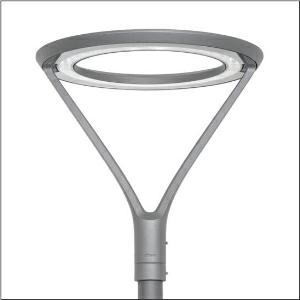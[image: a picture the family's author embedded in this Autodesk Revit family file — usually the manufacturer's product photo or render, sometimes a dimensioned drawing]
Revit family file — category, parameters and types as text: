
# Revit family: dl_r__20___pl1_2s_5xa512832s008_323f
name_source: partatom
category: Lighting Fixtures
units: mm (PartAtom-declared; Revit-internal decimal feet)

## family parameters
Cut with Voids When Loaded = No
Host = Face
Light Source = No
Part Type = Normal
Room Calculation Point = No
Round Connector Dimension = Use Diameter
Shared = No

## types (1)
- --- (1 x LED, 3050 lm, 30.4 W, 2200K)
    Apparent Load = 30 VA
    CIE Flux Codes = 33 78 99 100 100
    Color Rendering = 70
    Color Temperature = 2200K
    Default Elevation = 1800 mm
    Description = DL® 20, mast luminaire, primary light control with reflector, highly specular, primary optical cover: cover, of toughened safety glass of clear glass with excellent transmission level, light distribution: PL1.2s, light emission: direct distribution, primary light characteristic: symmetric, installation type: post-top, LED, High Power LED, rated luminous flux: 3.040lm, luminous efficacy: 86lm/W, light colour: 722, colour temperature: 2200K, control gear: ECG Plus, control: flexible luminous flux parameterisation, time-dependent luminous flux control, constant luminous flux control, digital communication interface, power reduction, overheat protection, electronic power reduction, mains connection: 230..240V, 50/60Hz, connection cable pre-assembled, cable length: 5m, start of lifetime: 36W, end of service life: 36W, reduction: 17W, luminaire housing, upper part, of cast aluminium, powder-coated, Siteco® metallic grey (DB 702S), diameter: 690mm, height: 690mm, spigot size: 76mm (post-top), luminaire housing, of cast aluminium, powder-coated, Siteco® metallic grey (DB 702S), equipment: standard, protection rating (complete): IP66, insulation class (complete): insulation class II (safety insulation), certification: CE, ENEC, VDE, impact resistance: IK08, permissible operating ambient temperature: -25..+35°C, standard-compliant lighting for roads and squares, packaging unit: 1 piece

Light Distribution: PL1.2s
    Height = 690 mm
    Lamp = 1 x LED
    Lamp Light Flux = 3050 lm
    Lamp Power = 30.4 W
    Lamp count = 1
    Length = 690 mm
    Luminous efficacy = 100 lm/W
    Manufacturer = Siteco
    ModVariant = No
    Model = 5XA512832S008
    Number of Poles = 1
    OnlyDefault = Yes
    Power Factor = 1
    Product Name = DL® 20 | PL1.2s
    Product group = mast luminaire | pylon top
    ProductGroupID = 6100
    Protection Class = Protection class II
    Protection Degree = IP 66
    RLX_Detail_Level = 1
    RLX_Emergency_Light_Flux = 0 lm
    RLX_Emergency_Type = 0
    RLX_Emergency_Type_DB = No
    RlxData = <blob elided: 203997 chars, md5=7cc40eea>
    Socket = socket
    Standby Power = 0 W
    System Light Flux = 3050 lm
    System Power = 30 W
    Type Comments = factory setting: luminous flux: 100 % | dim-lin: 254 | 412 mA
    Type Image = l_1006001.jpg
    URL = http://relux.com
    VarID = @adj_046029
    Voltage = 0 V
    Weight = 0.00 kg
    Width = 0 mm  [stored 0 ft]

note: [stored X ft] marks values corroborated as IEEE doubles in the binary element streams (Revit-internal decimal feet)

## geometry (parser evidence)
native form markers: Blend x4, Sweep x9
no freeform markers — native parametric forms only
